# Revit family: 57_ME_UN_HRC-425-570 links_Orcon
name_source: partatom
category: Mechanical Equipment
units: mm (PartAtom-declared; Revit-internal decimal feet)

## family parameters
Always vertical = Yes
Cut with Voids When Loaded = No
OmniClass Number = 23.75.10.34.21
OmniClass Title = Heat Exchangers for Ventilation Air
Part Type = Normal
Room Calculation Point = No
Round Connector Dimension = Use Diameter
Shared = No
Work Plane-Based = No

## types (4) — shared parameters
Black = Color RGB 076-076-076
Blue = Color RGB 000-137-182
ClassificationCode = 57.52
Depth = 605 mm  [stored 1.98491 ft]
Description = WTW unit
Diameter Inner = 148 mm
Duct Diameter 1 = 160 mm  [stored 0.524934 ft]
GLN = 8718403860009
Grey = Color RGB 128-128-128
Height = 877 mm  [stored 2.8773 ft]
Hertz = 50 Hz
IFCExportAs = IfcHeatExchanger
IFCExportType = NOTDEFINED
Manufacturer = Orcon
Power = 73 VA
Return Angle = 90.00°
Return Side Cap = Yes
Return Top Cap = No
Return Top Connection = Yes
Sanitary Diameter = 32 mm  [stored 0.104987 ft]
Supply1 Angle = 90.00°
Supply1 Side Cap = Yes
Supply1 Top Cap = No
Supply1 Top Connection = Yes
Unit Weight (kg) = 34
Voltage = 230 V
White = Color RAL 9016
White Body = Color RGB 250-250-250
Width = 760 mm  [stored 2.49344 ft]
zero-valued in all types: Default Elevation

## per-type parameters (varying)
| type | Airflow Rate (m3/h) | Duct Diameter 2 | GTIN | URL | artikelnummer |
| HRC-425-EcoSmart | 425 | 160 mm  [stored 0.524934 ft] | 8718403863383 | https://www.orcon.nl | 22001090 |
| HRC-425-SmartComfort | 425 | 160 mm  [stored 0.524934 ft] | 8718403863390 |  | 22001095 |
| HRC-570-EcoSmart | 570 | 180 mm  [stored 0.590551 ft] | 8718403863406 |  | 22001100 |
| HRC-570-SmartComfort | 570 | 180 mm  [stored 0.590551 ft] | 8718403863413 |  | 22001105 |

note: column(s) folded — value = type name in every type: Model

note: [stored X ft] marks values corroborated as IEEE doubles in the binary element streams (Revit-internal decimal feet)

## geometry (parser evidence)
native form markers: Sweep x10
no freeform markers — native parametric forms only
